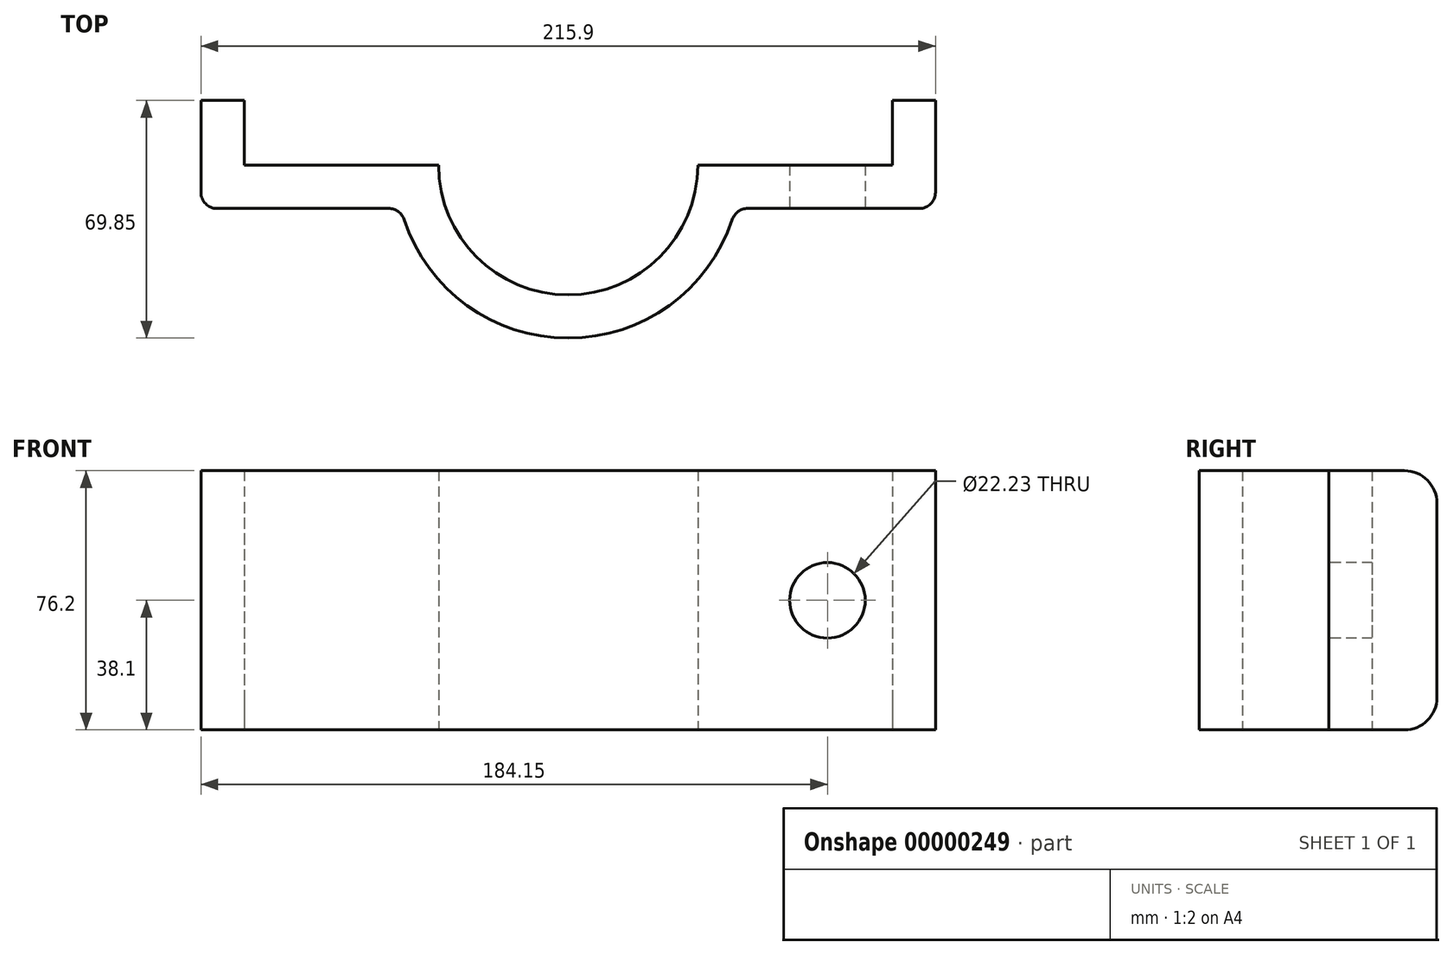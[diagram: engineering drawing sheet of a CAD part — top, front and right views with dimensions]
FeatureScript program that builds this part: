
annotation { "Feature Type Name" : "Feature", "Feature Type Description" : "" }
export const myFeature = defineFeature(function(context is Context, id is Id, definition is map)
    precondition{}
    {
        {
            var Q0;
            Q0=qCreatedBy(makeId("Top.planeOp"),FACE);
            var sketch = newSketch(context, id + "F0", { "sketchPlane" : qUnion([Q0])});
            skArc(sketch, "E0", {"start": v(-38.1, 0) * mm, "mid": v(0, -38.1) * mm, "end": v(38.1, 0) * mm});
            skArc(sketch, "E1", {"start": v(-49.19, -12.7) * mm, "mid": v(0, -50.8) * mm, "end": v(49.19, -12.7) * mm});
            skLineSegment(sketch, "E2", {"start": v(-38.1, 0) * mm, "end": v(-95.25, 0) * mm});
            skLineSegment(sketch, "E3", {"start": v(-95.25, 0) * mm, "end": v(-95.25, 19.05) * mm});
            skLineSegment(sketch, "E4", {"start": v(-95.25, 19.05) * mm, "end": v(-107.95, 19.05) * mm});
            skLineSegment(sketch, "E5", {"start": v(-107.95, 19.05) * mm, "end": v(-107.95, -12.7) * mm});
            skLineSegment(sketch, "E6", {"start": v(-107.95, -12.7) * mm, "end": v(-49.19, -12.7) * mm});
            skLineSegment(sketch, "E7", {"start": v(0, 0) * mm, "end": v(-95.25, 0) * mm, "construction": true});
            skLineSegment(sketch, "E8", {"start": v(0, 59.15) * mm, "end": v(0, -77.7) * mm, "construction": true});
            skLineSegment(sketch, "E9.0.MirrorCS", {"start": v(38.1, 0) * mm, "end": v(95.25, 0) * mm});
            skLineSegment(sketch, "E10.0.MirrorCS", {"start": v(107.95, -12.7) * mm, "end": v(49.19, -12.7) * mm});
            skLineSegment(sketch, "E11.0.MirrorCS", {"start": v(95.25, 0) * mm, "end": v(95.25, 19.05) * mm});
            skLineSegment(sketch, "E12.0.MirrorCS", {"start": v(95.25, 19.05) * mm, "end": v(107.95, 19.05) * mm});
            skLineSegment(sketch, "E13.0.MirrorCS", {"start": v(107.95, 19.05) * mm, "end": v(107.95, -12.7) * mm});
            skSolve(sketch);
        }
        {
            var Q0;
            Q0=makeQuery(id+"F0.imprint","IMPRINT",FACE,{"disambiguationData":[TD([[makeQuery(id+"F0.imprint","IMPRINT",EDGE,{"derivedFrom":sQuery(id+"F0.wireOp",EDGE,"E0")}),-1.0]])]});
            extrude(context, id + "F1", {"entities" : qUnion([Q0]), "depth" : 76.2 * mm});
        }
        {
            var Q0;
            Q0=makeQuery(id+"F1.opExtrude","SWEPT_EDGE",EDGE,{"disambiguationData":[OSD([sQuery(id+"F0.wireOp",EDGE,"E1"),sQuery(id+"F0.wireOp",EDGE,"E10.0.MirrorCS")])]});
            var Q1;
            Q1=makeQuery(id+"F1.opExtrude","SWEPT_EDGE",EDGE,{"disambiguationData":[OSD([sQuery(id+"F0.wireOp",EDGE,"E10.0.MirrorCS"),sQuery(id+"F0.wireOp",EDGE,"E13.0.MirrorCS")])]});
            var Q2;
            Q2=makeQuery(id+"F1.opExtrude","SWEPT_EDGE",EDGE,{"disambiguationData":[OSD([sQuery(id+"F0.wireOp",EDGE,"E1"),sQuery(id+"F0.wireOp",EDGE,"E6")])]});
            var Q3;
            Q3=makeQuery(id+"F1.opExtrude","SWEPT_EDGE",EDGE,{"disambiguationData":[OSD([sQuery(id+"F0.wireOp",EDGE,"E5"),sQuery(id+"F0.wireOp",EDGE,"E6")])]});
            fillet(context, id + "F2", {"entities" : qUnion([Q0, Q1, Q2, Q3]), "radius" : 4.76 * mm, "tangentPropagation" : true, "allowEdgeOverflow" : false});
        }
        {
            var Q0;
            Q0=makeQuery(id+"F1.opExtrude","CAP_EDGE",EDGE,{"disambiguationData":[OSD([sQuery(id+"F0.wireOp",EDGE,"E4")])],"isStart":false});
            var Q1;
            Q1=makeQuery(id+"F1.opExtrude","CAP_EDGE",EDGE,{"disambiguationData":[OSD([sQuery(id+"F0.wireOp",EDGE,"E12.0.MirrorCS")])],"isStart":false});
            var Q2;
            Q2=makeQuery(id+"F1.opExtrude","CAP_EDGE",EDGE,{"disambiguationData":[OSD([sQuery(id+"F0.wireOp",EDGE,"E12.0.MirrorCS")])],"isStart":true});
            var Q3;
            Q3=makeQuery(id+"F1.opExtrude","CAP_EDGE",EDGE,{"disambiguationData":[OSD([sQuery(id+"F0.wireOp",EDGE,"E4")])],"isStart":true});
            fillet(context, id + "F3", {"entities" : qUnion([Q0, Q1, Q2, Q3]), "radius" : 9.52 * mm, "tangentPropagation" : true, "allowEdgeOverflow" : false});
        }
        {
            var Q0;
            Q0=makeQuery(id+"F1.opExtrude","SWEPT_FACE",FACE,{"disambiguationData":[OSD([sQuery(id+"F0.wireOp",EDGE,"E10.0.MirrorCS")])]});
            var sketch = newSketch(context, id + "F4", { "sketchPlane" : qUnion([Q0])});
            skLineSegment(sketch, "E14", {"start": v(0, 0) * mm, "end": v(76.2, 0) * mm, "construction": true});
            skCircle(sketch, "E15", {"center": v(76.2, 38.1) * mm, "radius": 11.11 * mm});
            skLineSegment(sketch, "E16", {"start": v(0, 0) * mm, "end": v(0, 76.38) * mm, "construction": true});
            skCircle(sketch, "E17.0.MirrorC", {"center": v(-76.2, 38.1) * mm, "radius": 11.11 * mm});
            skSolve(sketch);
        }
        {
            var Q0;
            {Q0=qUnion([makeQuery(id+"F4.imprint","IMPRINT",FACE,{"disambiguationData":[TD([[makeQuery(id+"F4.imprint","IMPRINT",EDGE,{"derivedFrom":sQuery(id+"F4.wireOp",EDGE,"E17.0.MirrorC")}),-1.0]])]}),makeQuery(id+"F4.imprint","IMPRINT",FACE,{"disambiguationData":[TD([[makeQuery(id+"F4.imprint","IMPRINT",EDGE,{"derivedFrom":sQuery(id+"F4.wireOp",EDGE,"E15")}),1.0]])]})]);}
            extrude(context, id + "F5", {"entities" : qUnion([Q0]), "operationType" : NewBodyOperationType.REMOVE, "endBound" : BoundingType.THROUGH_ALL, "oppositeDirection" : true, "depth" : 25.4 * mm});
        }
    });
